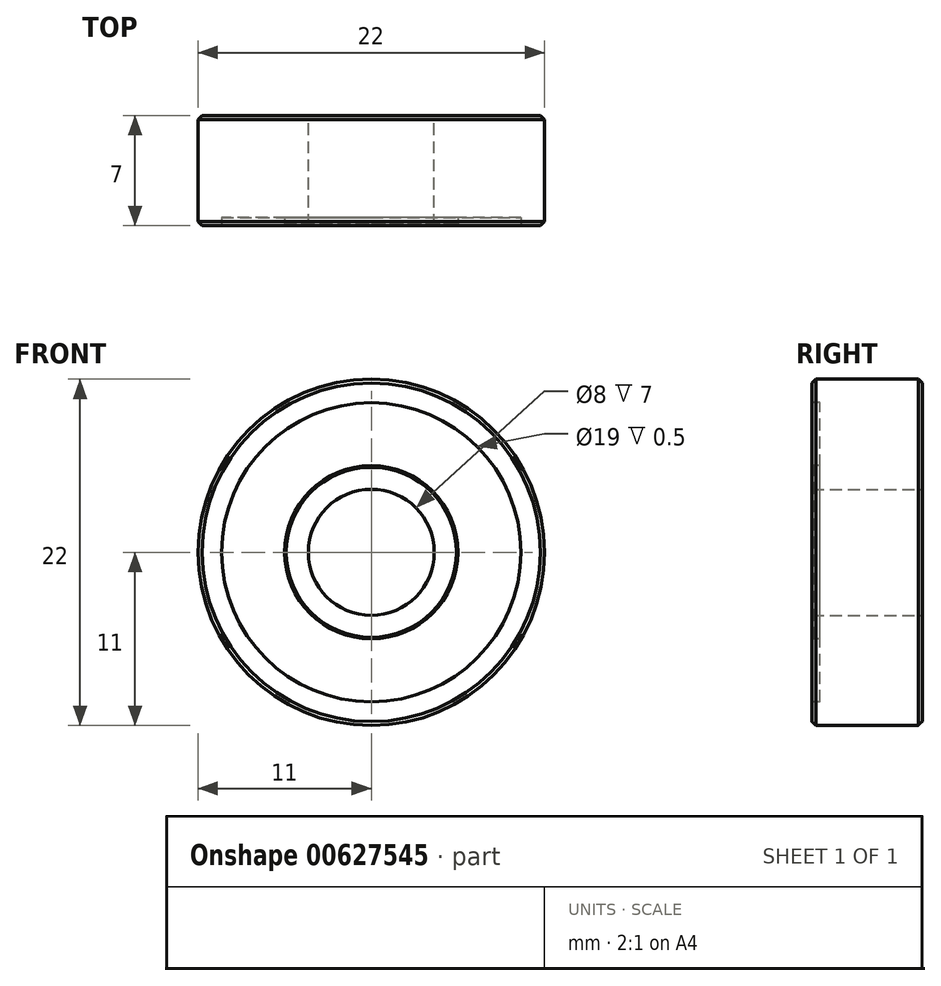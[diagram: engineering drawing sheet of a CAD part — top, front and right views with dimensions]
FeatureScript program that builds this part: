
annotation { "Feature Type Name" : "Feature", "Feature Type Description" : "" }
export const myFeature = defineFeature(function(context is Context, id is Id, definition is map)
    precondition{}
    {
        {
            var Q0;
            Q0=qCreatedBy(makeId("Front.planeOp"),FACE);
            var sketch = newSketch(context, id + "F0", { "sketchPlane" : qUnion([Q0])});
            skCircle(sketch, "E0", {"center": v(0, 0) * mm, "radius": 11 * mm});
            skCircle(sketch, "E1", {"center": v(0, 0) * mm, "radius": 4 * mm});
            skSolve(sketch);
        }
        {
            var Q0;
            Q0=makeQuery(id+"F0.imprint","IMPRINT",FACE,{"disambiguationData":[TD([[makeQuery(id+"F0.imprint","IMPRINT",EDGE,{"derivedFrom":sQuery(id+"F0.wireOp",EDGE,"E0")}),1.0]])]});
            extrude(context, id + "F1", {"entities" : qUnion([Q0]), "endBound" : BoundingType.SYMMETRIC, "depth" : 7 * mm, "offsetDistance" : 25 * mm});
        }
        {
            var Q0;
            Q0=makeQuery(id+"F1.opExtrude","CAP_FACE",FACE,{"disambiguationData":[OSD([sQuery(id+"F0.wireOp",EDGE,"E0"),sQuery(id+"F0.wireOp",EDGE,"E1")])],"isStart":false});
            var sketch = newSketch(context, id + "F2", { "sketchPlane" : qUnion([Q0])});
            skCircle(sketch, "E2.0", {"center": v(0, 0) * mm, "radius": 9.5 * mm});
            skCircle(sketch, "E3.0", {"center": v(0, 0) * mm, "radius": 5.5 * mm});
            skSolve(sketch);
        }
        {
            var Q0;
            Q0=qSketchRegion(id+"F2",true);
            extrude(context, id + "F3", {"entities" : qUnion([Q0]), "operationType" : NewBodyOperationType.REMOVE, "oppositeDirection" : true, "depth" : 0.5 * mm, "offsetDistance" : 25 * mm});
        }
        {
            var Q0;
            Q0=makeQuery(id+"F1.opExtrude","CAP_EDGE",EDGE,{"disambiguationData":[OSD([sQuery(id+"F0.wireOp",EDGE,"E0")])],"isStart":false});
            var Q1;
            Q1=makeQuery(id+"F1.opExtrude","CAP_EDGE",EDGE,{"disambiguationData":[OSD([sQuery(id+"F0.wireOp",EDGE,"E0")])],"isStart":true});
            chamfer(context, id + "F4", {"entities" : qUnion([Q0, Q1]), "width" : 0.25 * mm, "tangentPropagation" : true});
        }
        {
            var Q0;
            Q0=makeQuery(id+"F3.boolean.opBoolean","COPY",EDGE,{"derivedFrom":makeQuery(id+"F3.opExtrude","CAP_EDGE",EDGE,{"disambiguationData":[OSD([sQuery(id+"F2.wireOp",EDGE,"E2.0")])],"isStart":true})});
            var Q1;
            Q1=makeQuery(id+"F3.boolean.opBoolean","COPY",EDGE,{"derivedFrom":makeQuery(id+"F3.opExtrude","CAP_EDGE",EDGE,{"disambiguationData":[OSD([sQuery(id+"F2.wireOp",EDGE,"E3.0")])],"isStart":true})});
            var Q2;
            Q2=makeQuery(id+"FeYEaoZEhtLTkzV_1.1.F3.boolean.opBoolean","COPY",EDGE,{"derivedFrom":makeQuery(id+"FeYEaoZEhtLTkzV_1.1.F3.opExtrude","CAP_EDGE",EDGE,{"disambiguationData":[OSD([sQuery(id+"F2.wireOp",EDGE,"E2.0")])],"isStart":true})});
            var Q3;
            Q3=makeQuery(id+"FeYEaoZEhtLTkzV_1.1.F3.boolean.opBoolean","COPY",EDGE,{"derivedFrom":makeQuery(id+"FeYEaoZEhtLTkzV_1.1.F3.opExtrude","CAP_EDGE",EDGE,{"disambiguationData":[OSD([sQuery(id+"F2.wireOp",EDGE,"E3.0")])],"isStart":true})});
            chamfer(context, id + "F5", {"entities" : qUnion([Q0, Q1, Q2, Q3]), "width" : 0.1 * mm, "tangentPropagation" : true});
        }
    });
